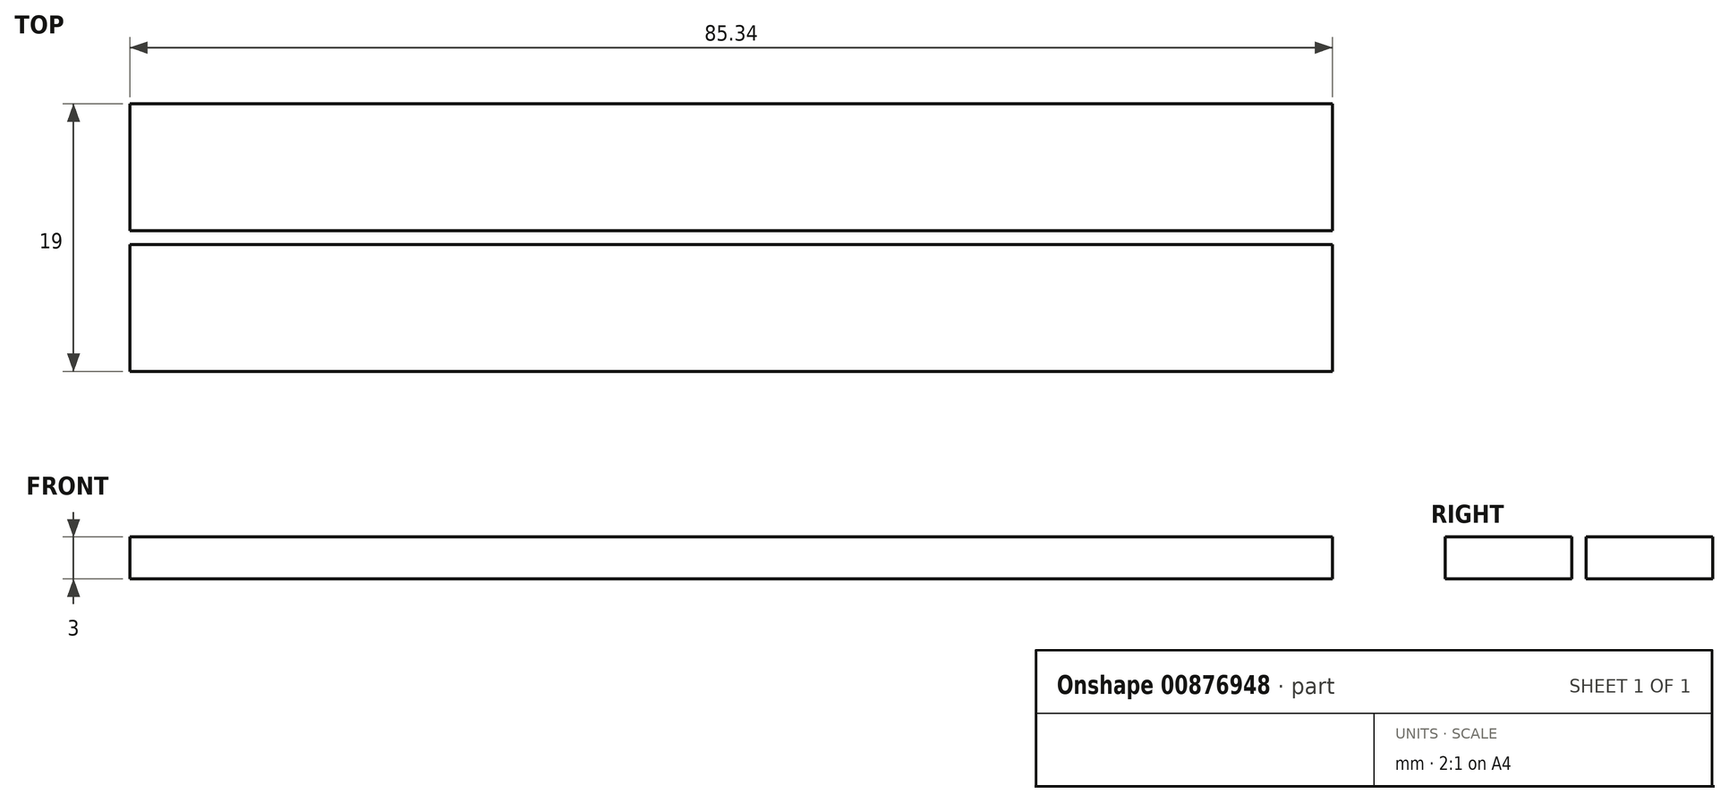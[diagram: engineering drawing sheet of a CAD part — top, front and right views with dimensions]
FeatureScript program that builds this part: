
annotation { "Feature Type Name" : "Feature", "Feature Type Description" : "" }
export const myFeature = defineFeature(function(context is Context, id is Id, definition is map)
    precondition{}
    {
        {
            var Q0;
            Q0=qCreatedBy(makeId("Top.planeOp"),FACE);
            var sketch = newSketch(context, id + "F0", { "sketchPlane" : qUnion([Q0])});
            skLineSegment(sketch, "E0.bottom", {"start": v(0, 0) * mm, "end": v(85.34, 0) * mm});
            skLineSegment(sketch, "E0.top", {"start": v(0, 9) * mm, "end": v(85.34, 9) * mm});
            skLineSegment(sketch, "E0.left", {"start": v(0, 0) * mm, "end": v(0, 9) * mm});
            skLineSegment(sketch, "E0.right", {"start": v(85.34, 0) * mm, "end": v(85.34, 9) * mm});
            skLineSegment(sketch, "E1.0.1.0", {"start": v(0, 19) * mm, "end": v(85.34, 19) * mm});
            skLineSegment(sketch, "E1.0.1.1", {"start": v(0, 10) * mm, "end": v(0, 19) * mm});
            skLineSegment(sketch, "E1.0.1.2", {"start": v(0, 10) * mm, "end": v(85.34, 10) * mm});
            skLineSegment(sketch, "E1.0.1.3", {"start": v(85.34, 10) * mm, "end": v(85.34, 19) * mm});
            skLineSegment(sketch, "E1.direction1", {"start": v(0, 9) * mm, "end": v(25, 9) * mm, "construction": true});
            skLineSegment(sketch, "E1.direction2", {"start": v(0, 9) * mm, "end": v(0, 19) * mm, "construction": true});
            skSolve(sketch);
        }
        {
            var Q0;
            Q0 = qSketchRegion(id + "F0", true);
            extrude(context, id + "F1", {"entities" : qUnion([Q0]), "depth" : 3 * mm, "offsetDistance" : 25 * mm});
        }
    });
